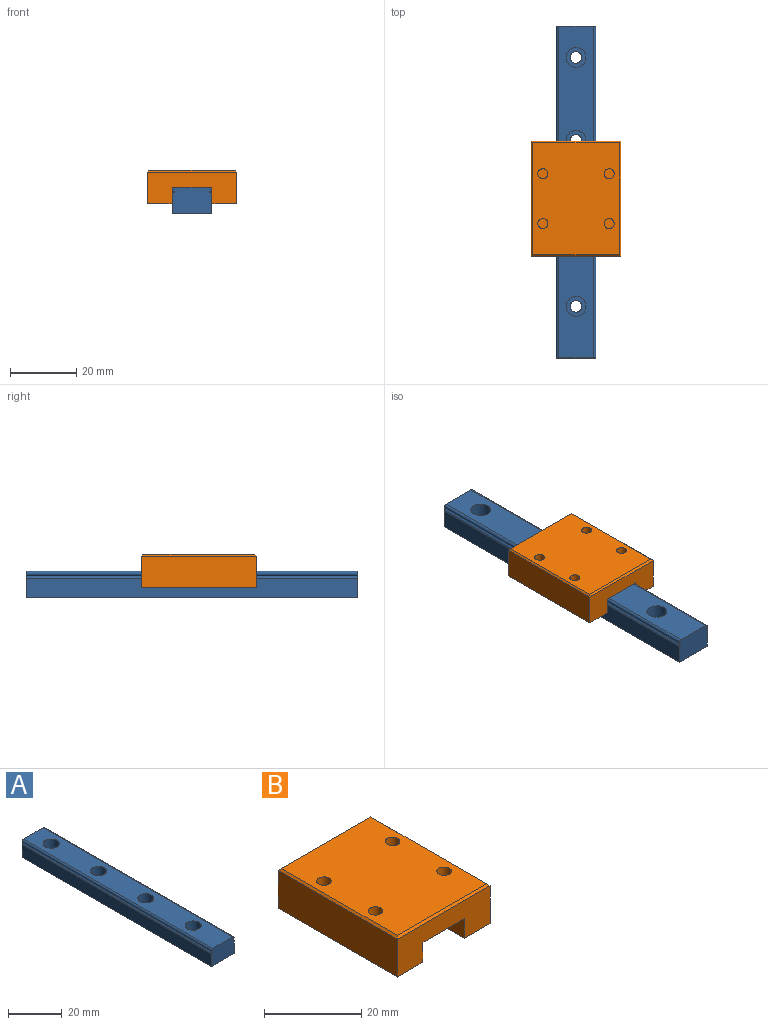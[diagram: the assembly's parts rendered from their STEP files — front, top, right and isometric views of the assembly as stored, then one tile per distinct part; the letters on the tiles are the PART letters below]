
ASSEMBLY  parts=2 mates=1
PART A: 22 faces, bbox 12x100x8 mm
  f0: cylinder r=0.75mm len=100mm, axis (0,-1,0), area 117.8mm2, adj f1,f7,f8,f9
  f1: cylinder r=0.75mm len=100mm, axis (0,-1,0), area 235.6mm2, adj f0,f2,f8,f9
  f2: plane 100x10.5mm, normal (0,0,1), area 936.9mm2, adj f1,f3,f8,f9,f12,f15,f18,f21
  f3: cylinder r=0.75mm len=100mm, axis (0,-1,0), area 235.6mm2, adj f2,f4,f8,f9
  f4: cylinder r=0.75mm len=100mm, axis (0,-1,0), area 117.8mm2, adj f3,f5,f8,f9
  f5: plane 100x5.75mm, normal (-1,0,0), area 575mm2, adj f4,f6,f8,f9
  f6: plane 100x12mm, normal (0,0,-1), area 1161.5mm2, adj f5,f7,f8,f9,f10,f13,f16,f19
  f7: plane 100x5.75mm, normal (1,0,0), area 575mm2, adj f0,f6,f8,f9
  f8: plane 12x8mm, normal (0,1,0), area 95.3mm2, adj f0,f1,f2,f3,f4,f5,f6,f7
  f9: plane 12x8mm, normal (0,-1,0), area 95.3mm2, adj f0,f1,f2,f3,f4,f5,f6,f7
  f10: cylinder r=1.75mm len=3.5mm, axis (0,0,1), area 38.5mm2, adj f6,f11
  f11: plane 6x6mm, normal (0,0,1), area 18.7mm2, adj f10,f12
  f12: cylinder r=3mm len=6mm, axis (0,0,1), area 84.8mm2, adj f2,f11
  f13: cylinder r=1.75mm len=3.5mm, axis (0,0,1), area 38.5mm2, adj f6,f14
  f14: plane 6x6mm, normal (0,0,1), area 18.7mm2, adj f13,f15
  f15: cylinder r=3mm len=6mm, axis (0,0,1), area 84.8mm2, adj f2,f14
  f16: cylinder r=1.75mm len=3.5mm, axis (0,0,1), area 38.5mm2, adj f6,f17
  f17: plane 6x6mm, normal (0,0,1), area 18.7mm2, adj f16,f18
  f18: cylinder r=3mm len=6mm, axis (0,0,1), area 84.8mm2, adj f2,f17
  f19: cylinder r=1.75mm len=3.5mm, axis (0,0,1), area 38.5mm2, adj f6,f20
  f20: plane 6x6mm, normal (0,0,1), area 18.7mm2, adj f19,f21
  f21: cylinder r=3mm len=6mm, axis (0,0,1), area 84.8mm2, adj f2,f20
PART B: 22 faces, bbox 27x34.7x10 mm
  f0: plane 27x9.5mm, normal (0,1,0), area 196.5mm2, adj f1,f2,f3,f4,f5,f9,f10,f11
  f1: plane 27x0.5mm, normal (0,0.71,0.71), area 18.7mm2, adj f0,f6,f7,f8
  f2: plane 34.7x12mm, normal (0,0,-1), area 416.4mm2, adj f0,f3,f4,f20
  f3: plane 34.7x5mm, normal (1,0,0), area 173.5mm2, adj f0,f2,f5,f20
  f4: plane 34.7x5mm, normal (-1,0,0), area 173.5mm2, adj f0,f2,f11,f20
  f5: plane 34.7x7.5mm, normal (0,0,-1), area 260.2mm2, adj f0,f3,f9,f20
  f6: plane 34.7x0.5mm, normal (0.71,0,0.71), area 24.2mm2, adj f1,f8,f10,f21
  f7: plane 34.7x0.5mm, normal (-0.71,0,0.71), area 24.2mm2, adj f1,f8,f9,f21
  f8: plane 33.7x26mm, normal (0,0,1), area 847.9mm2, adj f1,f6,f7,f12,f14,f16,f18,f21
  f9: plane 34.7x9.5mm, normal (-1,0,0), area 329.6mm2, adj f0,f5,f7,f20
  f10: plane 34.7x9.5mm, normal (1,0,0), area 329.6mm2, adj f0,f6,f11,f20
  f11: plane 34.7x7.5mm, normal (0,0,-1), area 260.3mm2, adj f0,f4,f10,f20
  f12: cylinder r=1.5mm len=3.5mm, axis (0,0,1), area 33mm2, adj f8,f13
  f13: plane 3x3mm, normal (0,0,1), area 7.1mm2, adj f12
  f14: cylinder r=1.5mm len=3.5mm, axis (0,0,1), area 33mm2, adj f8,f15
  f15: plane 3x3mm, normal (0,0,1), area 7.1mm2, adj f14
  f16: cylinder r=1.5mm len=3.5mm, axis (0,0,1), area 33mm2, adj f8,f17
  f17: plane 3x3mm, normal (0,0,1), area 7.1mm2, adj f16
  f18: cylinder r=1.5mm len=3.5mm, axis (0,0,1), area 33mm2, adj f8,f19
  f19: plane 3x3mm, normal (0,0,1), area 7.1mm2, adj f18
  f20: plane 27x9.5mm, normal (0,-1,0), area 196.5mm2, adj f2,f3,f4,f5,f9,f10,f11,f21
  f21: plane 27x0.5mm, normal (0,-0.71,0.71), area 18.7mm2, adj f6,f7,f8,f20
PLACE A t=(6.96,-94.99,1.29)mm fixed
PLACE B rot(axis=(0,0,1),180deg) t=(6.96,-47.02,0.29)mm
MATE slider B.f0 <-> A.f9  axis (0,-1,0) through (6.96,-64.37,5.29)mm
